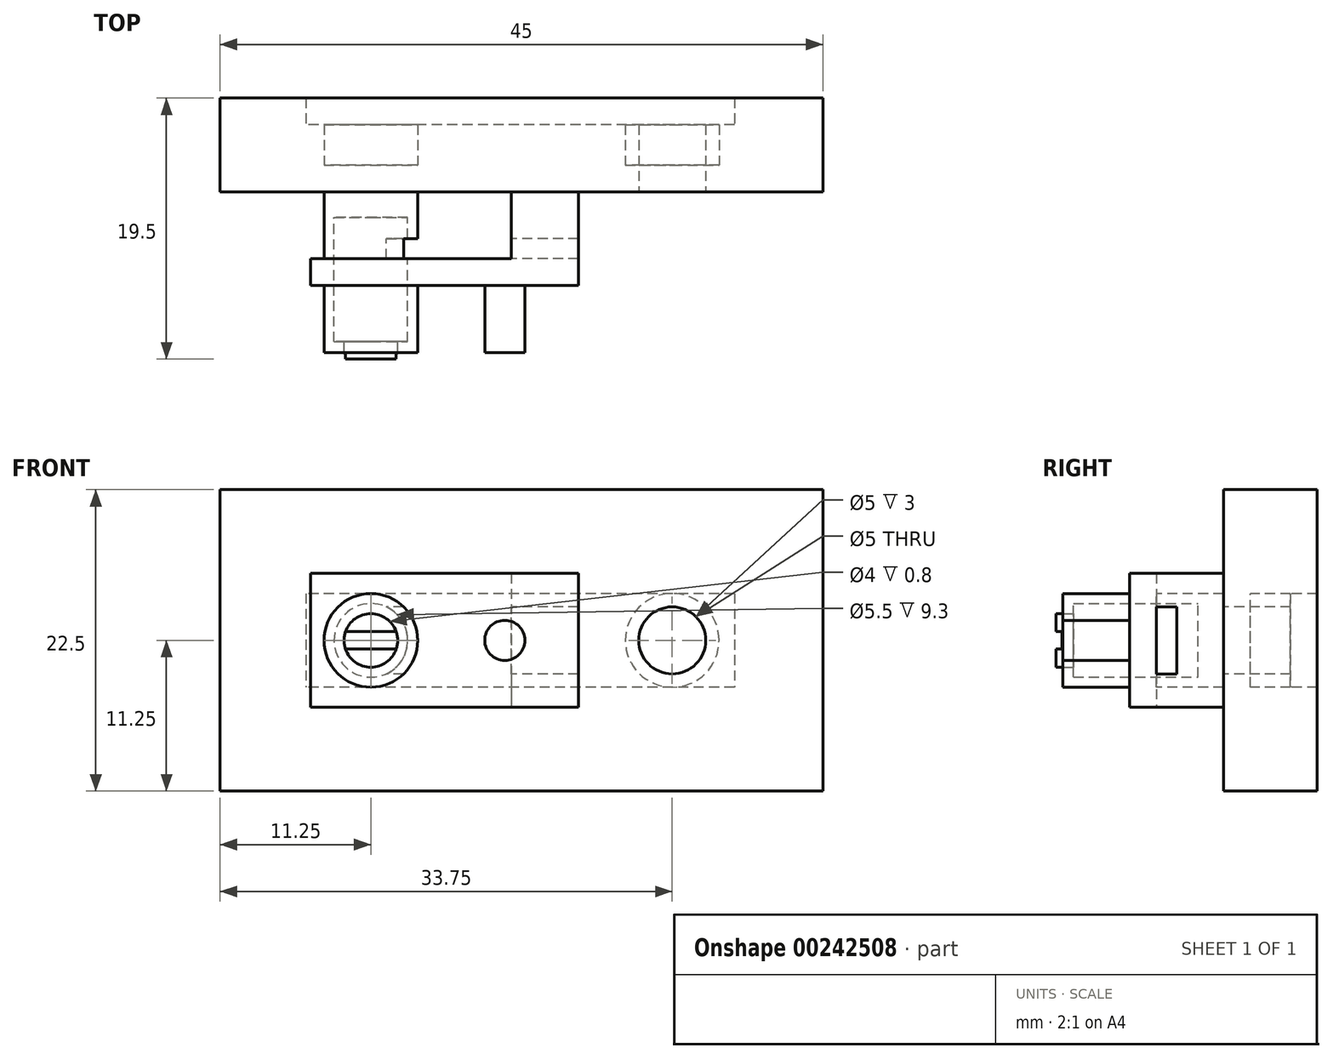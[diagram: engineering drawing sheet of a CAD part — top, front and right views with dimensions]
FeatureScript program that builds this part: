
annotation { "Feature Type Name" : "Feature", "Feature Type Description" : "" }
export const myFeature = defineFeature(function(context is Context, id is Id, definition is map)
    precondition{}
    {
        {
            var Q0;
            Q0=qCreatedBy(makeId("Front.planeOp"),FACE);
            var sketch = newSketch(context, id + "F0", { "sketchPlane" : qUnion([Q0])});
            skCircle(sketch, "E0", {"center": v(0, 0) * mm, "radius": 2.75 * mm});
            skSolve(sketch);
        }
        {
            var Q0;
            Q0 = qSketchRegion(id + "F0", true);
            extrude(context, id + "F1", {"entities" : qUnion([Q0]), "depth" : 7 * mm, "offsetDistance" : 25 * mm});
        }
        {
            var Q0;
            Q0=qCreatedBy(makeId("Front.planeOp"),FACE);
            var sketch = newSketch(context, id + "F2", { "sketchPlane" : qUnion([Q0])});
            skCircle(sketch, "E1", {"center": v(0, 0) * mm, "radius": 2 * mm});
            skSolve(sketch);
        }
        {
            var Q0;
            Q0 = qSketchRegion(id + "F2", true);
            extrude(context, id + "F3", {"entities" : qUnion([Q0]), "operationType" : NewBodyOperationType.REMOVE, "depth" : 9.9 * mm, "offsetDistance" : 25 * mm, "hasSecondDirection" : true, "secondDirectionOppositeDirection" : true, "secondDirectionDepth" : 12.8 * mm});
        }
        {
            var Q0;
            Q0=qCreatedBy(makeId("Front.planeOp"),FACE);
            var sketch = newSketch(context, id + "F4", { "sketchPlane" : qUnion([Q0])});
            skCircle(sketch, "E2", {"center": v(0, 0) * mm, "radius": 3.5 * mm});
            skSolve(sketch);
        }
        {
            var Q0;
            Q0=makeQuery(id+"F4.imprint","IMPRINT",FACE,{"disambiguationData":[TD([[makeQuery(id+"F4.imprint","IMPRINT",EDGE,{"derivedFrom":sQuery(id+"F4.wireOp",EDGE,"E2")}),1.0]])]});
            extrude(context, id + "F5", {"entities" : qUnion([Q0]), "operationType" : NewBodyOperationType.ADD, "oppositeDirection" : true, "depth" : 5 * mm, "offsetDistance" : 25 * mm});
        }
        {
            var Q0;
            Q0=qCreatedBy(makeId("Front.planeOp"),FACE);
            var sketch = newSketch(context, id + "F6", { "sketchPlane" : qUnion([Q0])});
            skCircle(sketch, "E3", {"center": v(0, 0) * mm, "radius": 2 * mm});
            skSolve(sketch);
        }
        {
            var Q0;
            Q0 = qSketchRegion(id + "F6", true);
            extrude(context, id + "F7", {"entities" : qUnion([Q0]), "depth" : 7.5 * mm, "offsetDistance" : 25 * mm});
        }
        {
            var Q0;
            Q0=qCreatedBy(makeId("Front.planeOp"),FACE);
            var sketch = newSketch(context, id + "F8", { "sketchPlane" : qUnion([Q0])});
            skLineSegment(sketch, "E4.bottom", {"start": v(-2, 0.65) * mm, "end": v(2, 0.65) * mm});
            skLineSegment(sketch, "E4.top", {"start": v(-2, -0.65) * mm, "end": v(2, -0.65) * mm});
            skLineSegment(sketch, "E4.left", {"start": v(-2, 0.65) * mm, "end": v(-2, -0.65) * mm});
            skLineSegment(sketch, "E4.right", {"start": v(2, 0.65) * mm, "end": v(2, -0.65) * mm});
            skPoint(sketch, "E4.middle", {"position": v(0, 0) * mm});
            skSolve(sketch);
        }
        {
            var Q0;
            Q0 = qSketchRegion(id + "F8", true);
            extrude(context, id + "F9", {"entities" : qUnion([Q0]), "operationType" : NewBodyOperationType.REMOVE, "depth" : 9.05 * mm, "offsetDistance" : 25 * mm, "hasSecondDirection" : true, "secondDirectionOppositeDirection" : false, "secondDirectionDepth" : 7.05 * mm});
        }
        {
            var Q0;
            Q0=qCreatedBy(makeId("Front.planeOp"),FACE);
            var sketch = newSketch(context, id + "F10", { "sketchPlane" : qUnion([Q0])});
            skLineSegment(sketch, "E5.bottom", {"start": v(-15.5, 5) * mm, "end": v(15.5, 5) * mm});
            skLineSegment(sketch, "E5.top", {"start": v(-15.5, -5) * mm, "end": v(15.5, -5) * mm});
            skLineSegment(sketch, "E5.left", {"start": v(-15.5, 5) * mm, "end": v(-15.5, -5) * mm});
            skLineSegment(sketch, "E5.right", {"start": v(15.5, 5) * mm, "end": v(15.5, -5) * mm});
            skPoint(sketch, "E5.middle", {"position": v(0, 0) * mm});
            skLineSegment(sketch, "E6", {"start": v(0, 5) * mm, "end": v(0, -5) * mm, "construction": true});
            skLineSegment(sketch, "E7", {"start": v(-4.5, 5) * mm, "end": v(-4.5, -5) * mm});
            skSolve(sketch);
        }
        {
            var Q0;
            {var subQ0=sQuery(id+"F10.wireOp",EDGE,"E5.right");Q0=makeQuery(id+"F10.imprint","IMPRINT",FACE,{"disambiguationData":[TD([[makeQuery(id+"F10.imprint","IMPRINT",EDGE,{"derivedFrom":subQ0}),-1.0]])]});}
            extrude(context, id + "F11", {"entities" : qUnion([Q0]), "depth" : 2 * mm, "offsetDistance" : 25 * mm});
        }
        {
            var Q0;
            Q0=qCreatedBy(makeId("Top.planeOp"),FACE);
            var sketch = newSketch(context, id + "F12", { "sketchPlane" : qUnion([Q0])});
            skLineSegment(sketch, "E8.bottom", {"start": v(10.5, 5) * mm, "end": v(15.5, 5) * mm});
            skLineSegment(sketch, "E8.top", {"start": v(10.5, 0) * mm, "end": v(15.5, 0) * mm});
            skLineSegment(sketch, "E8.left", {"start": v(10.5, 5) * mm, "end": v(10.5, 0) * mm});
            skLineSegment(sketch, "E8.right", {"start": v(15.5, 5) * mm, "end": v(15.5, 0) * mm});
            skSolve(sketch);
        }
        {
            var Q0;
            Q0 = qSketchRegion(id + "F12", true);
            extrude(context, id + "F13", {"entities" : qUnion([Q0]), "operationType" : NewBodyOperationType.ADD, "depth" : 10 * mm, "offsetDistance" : 25 * mm, "symmetric" : true});
        }
        {
            var Q0;
            Q0=qCreatedBy(makeId("Right.planeOp"),FACE);
            var sketch = newSketch(context, id + "F14", { "sketchPlane" : qUnion([Q0])});
            skLineSegment(sketch, "E9.bottom", {"start": v(0, 0) * mm, "end": v(1.5, 0) * mm});
            skLineSegment(sketch, "E9.top", {"start": v(0, 5) * mm, "end": v(1.5, 5) * mm});
            skLineSegment(sketch, "E9.left", {"start": v(0, 0) * mm, "end": v(0, 5) * mm});
            skLineSegment(sketch, "E9.right", {"start": v(1.5, 0) * mm, "end": v(1.5, 5) * mm});
            skLineSegment(sketch, "E10", {"start": v(0, -2.5) * mm, "end": v(1.5, -2.5) * mm});
            skLineSegment(sketch, "E11.MirrorCS", {"start": v(0, 2.5) * mm, "end": v(1.5, 2.5) * mm});
            skLineSegment(sketch, "E12.MirrorCS", {"start": v(1.5, 0) * mm, "end": v(1.5, -5) * mm});
            skLineSegment(sketch, "E13.MirrorCS", {"start": v(0, 0) * mm, "end": v(0, -5) * mm});
            skSolve(sketch);
        }
        {
            var Q0;
            {var subQ0=sQuery(id+"F14.wireOp",EDGE,"E9.bottom");Q0=makeQuery(id+"F14.imprint","IMPRINT",FACE,{"disambiguationData":[TD([[makeQuery(id+"F14.imprint","IMPRINT",EDGE,{"derivedFrom":subQ0}),-1.0]])]});}
            var Q1;
            {var subQ0=sQuery(id+"F14.wireOp",EDGE,"E9.bottom");Q1=makeQuery(id+"F14.imprint","IMPRINT",FACE,{"disambiguationData":[TD([[makeQuery(id+"F14.imprint","IMPRINT",EDGE,{"derivedFrom":subQ0}),1.0]])]});}
            extrude(context, id + "F15", {"entities" : qUnion([Q0, Q1]), "operationType" : NewBodyOperationType.REMOVE, "depth" : 22.67 * mm, "offsetDistance" : 25 * mm});
        }
        {
            var Q0;
            Q0=qCreatedBy(makeId("Front.planeOp"),FACE);
            var sketch = newSketch(context, id + "F16", { "sketchPlane" : qUnion([Q0])});
            skCircle(sketch, "E14", {"center": v(0, 0) * mm, "radius": 2.75 * mm});
            skCircle(sketch, "E15", {"center": v(0, 0) * mm, "radius": 3.5 * mm});
            skSolve(sketch);
        }
        {
            var Q0;
            Q0 = qSketchRegion(id + "F16", true);
            extrude(context, id + "F17", {"entities" : qUnion([Q0]), "operationType" : NewBodyOperationType.ADD, "depth" : 7 * mm, "offsetDistance" : 25 * mm});
        }
        {
            var Q0;
            Q0=qCreatedBy(makeId("Front.planeOp"),FACE);
            var sketch = newSketch(context, id + "F18", { "sketchPlane" : qUnion([Q0])});
            skCircle(sketch, "E16", {"center": v(0, 0) * mm, "radius": 2.75 * mm});
            skSolve(sketch);
        }
        {
            var Q0;
            Q0 = qSketchRegion(id + "F18", true);
            extrude(context, id + "F19", {"entities" : qUnion([Q0]), "operationType" : NewBodyOperationType.REMOVE, "depth" : 6.2 * mm, "offsetDistance" : 25 * mm, "hasSecondDirection" : true, "secondDirectionOppositeDirection" : true, "secondDirectionDepth" : 3.1 * mm});
        }
        {
            var Q0;
            Q0=qCreatedBy(makeId("Front.planeOp"),FACE);
            var sketch = newSketch(context, id + "F20", { "sketchPlane" : qUnion([Q0])});
            skCircle(sketch, "E17", {"center": v(10, 0) * mm, "radius": 1.5 * mm});
            skSolve(sketch);
        }
        {
            var Q0;
            Q0=qCreatedBy(makeId("Front.planeOp"),FACE);
            var sketch = newSketch(context, id + "F21", { "sketchPlane" : qUnion([Q0])});
            skCircle(sketch, "E18", {"center": v(0, 0) * mm, "radius": 9.75 * mm});
            skCircle(sketch, "E19", {"center": v(22.5, 0) * mm, "radius": 9.75 * mm});
            skSolve(sketch);
        }
        {
            var Q0;
            Q0=qCreatedBy(makeId("Front.planeOp"),FACE);
            var sketch = newSketch(context, id + "F22", { "sketchPlane" : qUnion([Q0])});
            skLineSegment(sketch, "E20", {"start": v(11.25, 0) * mm, "end": v(11.25, 23.72) * mm, "construction": true});
            skLineSegment(sketch, "E21.MirrorCS", {"start": v(11.25, 0) * mm, "end": v(11.25, -23.72) * mm, "construction": true});
            skLineSegment(sketch, "E22.bottom", {"start": v(11.25, 11.25) * mm, "end": v(33.75, 11.25) * mm});
            skLineSegment(sketch, "E22.top", {"start": v(11.25, -11.25) * mm, "end": v(33.75, -11.25) * mm});
            skLineSegment(sketch, "E22.left", {"start": v(11.25, 11.25) * mm, "end": v(11.25, -11.25) * mm, "construction": true});
            skLineSegment(sketch, "E22.right", {"start": v(33.75, 11.25) * mm, "end": v(33.75, -11.25) * mm});
            skLineSegment(sketch, "E23.MirrorCS", {"start": v(-11.25, 11.25) * mm, "end": v(-11.25, -11.25) * mm});
            skLineSegment(sketch, "E24.MirrorCS", {"start": v(11.25, 11.25) * mm, "end": v(-11.25, 11.25) * mm});
            skLineSegment(sketch, "E25.MirrorCS", {"start": v(11.25, -11.25) * mm, "end": v(-11.25, -11.25) * mm});
            skSolve(sketch);
        }
        {
            var Q0;
            Q0 = qSketchRegion(id + "F22", true);
            extrude(context, id + "F23", {"entities" : qUnion([Q0]), "oppositeDirection" : true, "depth" : 12 * mm, "offsetDistance" : 25 * mm, "hasSecondDirection" : true, "secondDirectionOppositeDirection" : true, "secondDirectionDepth" : 5 * mm});
        }
        {
            var Q0;
            Q0=qCreatedBy(makeId("Front.planeOp"),FACE);
            var sketch = newSketch(context, id + "F24", { "sketchPlane" : qUnion([Q0])});
            skCircle(sketch, "E26", {"center": v(0, 0) * mm, "radius": 3.5 * mm});
            skCircle(sketch, "E27", {"center": v(22.5, 0) * mm, "radius": 3.5 * mm});
            skSolve(sketch);
        }
        {
            var Q0;
            Q0 = qSketchRegion(id + "F24", true);
            extrude(context, id + "F25", {"entities" : qUnion([Q0]), "oppositeDirection" : true, "depth" : 14 * mm, "offsetDistance" : 25 * mm, "hasSecondDirection" : true, "secondDirectionOppositeDirection" : true, "secondDirectionDepth" : 7 * mm});
        }
        {
            var Q0;
            Q0=qCreatedBy(makeId("Front.planeOp"),FACE);
            var sketch = newSketch(context, id + "F26", { "sketchPlane" : qUnion([Q0])});
            skLineSegment(sketch, "E28", {"start": v(0, 0) * mm, "end": v(0, 11.15) * mm, "construction": true});
            skLineSegment(sketch, "E29", {"start": v(22.3, 0) * mm, "end": v(22.3, 12.16) * mm, "construction": true});
            skLineSegment(sketch, "E30", {"start": v(22.3, 0) * mm, "end": v(0, 0) * mm, "construction": true});
            skLineSegment(sketch, "E31", {"start": v(11.15, 11.96) * mm, "end": v(11.15, -11.35) * mm, "construction": true});
            skPoint(sketch, "E31.startSnap0", {"position": v(11.15, 0) * mm});
            skLineSegment(sketch, "E32.bottom", {"start": v(27.15, 3.5) * mm, "end": v(-4.85, 3.5) * mm});
            skLineSegment(sketch, "E32.top", {"start": v(27.15, -3.5) * mm, "end": v(-4.85, -3.5) * mm});
            skLineSegment(sketch, "E32.left", {"start": v(27.15, 3.5) * mm, "end": v(27.15, -3.5) * mm});
            skLineSegment(sketch, "E32.right", {"start": v(-4.85, 3.5) * mm, "end": v(-4.85, -3.5) * mm});
            skSolve(sketch);
        }
        {
            var Q0;
            Q0 = qSketchRegion(id + "F26", true);
            extrude(context, id + "F27", {"entities" : qUnion([Q0]), "operationType" : NewBodyOperationType.REMOVE, "oppositeDirection" : true, "depth" : 25 * mm, "offsetDistance" : 25 * mm, "hasSecondDirection" : true, "secondDirectionOppositeDirection" : true, "secondDirectionDepth" : 10 * mm});
        }
        {
            var Q0;
            Q0=makeQuery(id+"F20.imprint","IMPRINT",FACE,{"disambiguationData":[TD([[makeQuery(id+"F20.imprint","IMPRINT",EDGE,{"derivedFrom":sQuery(id+"F20.wireOp",EDGE,"E17")}),1.0]])]});
            var Q1;
            Q1=sQuery(id+"F20.wireOp",EDGE,"E17");
            extrude(context, id + "F28", {"entities" : qUnion([Q0]), "operationType" : NewBodyOperationType.ADD, "surfaceEntities" : qUnion([Q1]), "depth" : 7 * mm, "offsetDistance" : 25 * mm});
        }
        {
            var Q0;
            Q0=qCreatedBy(makeId("Front.planeOp"),FACE);
            var sketch = newSketch(context, id + "F29", { "sketchPlane" : qUnion([Q0])});
            skCircle(sketch, "E33", {"center": v(22.5, 0) * mm, "radius": 2.5 * mm});
            skSolve(sketch);
        }
        {
            var Q0;
            Q0=makeQuery(id+"F29.imprint","IMPRINT",FACE,{"disambiguationData":[TD([[makeQuery(id+"F29.imprint","IMPRINT",EDGE,{"derivedFrom":sQuery(id+"F29.wireOp",EDGE,"E33")}),1.0]])]});
            extrude(context, id + "F30", {"entities" : qUnion([Q0]), "operationType" : NewBodyOperationType.REMOVE, "oppositeDirection" : true, "depth" : 10 * mm, "offsetDistance" : 25 * mm});
        }
    });
